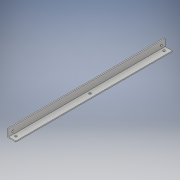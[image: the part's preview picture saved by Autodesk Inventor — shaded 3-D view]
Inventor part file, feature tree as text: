
AUTODESK INVENTOR PART (.ipt)
format: ipt  version: 2017 (Build 210142000, 142)  size: 129,024 bytes
history: native  units: in
note: dims shown in document units (in); Inventor stores cm internally (conversion verified against a paired STEP export)
features: hole x3, sketch x3, extrude x1
ambient origin geometry x8: Origin, YZ Plane, XZ Plane, XY Plane, X Axis, Y Axis, Z Axis, Center Point
bodies: Solid1 (feature_tree)
feature tree (7):
  extrude  "Extrusion1"  Depth=1.0in
  hole  "rail"  [1 undecoded]
  hole  "mount"  [1 undecoded]
  hole  "Hole5"  [1 undecoded]
  sketch  "Sketch2"  dims[d0=1.0in d1=1.0in]
  sketch  "Sketch7"  dims[d2=0.125in d3=19.375in d4=0.0in]
  sketch  "Sketch8"  dims[d5=0.5in d6=0.5in d7=0.7874in d9=18.375in d10=0.3937in d12=1.0in d14=0.266in d15=0.75in d16=0.385in d17=0.25in d18=0.5635in d19=1.0in d20=0.8108in d31=0.5in d43=0.5in d44=0.5in d45=0.7874in d47=18.375in d48=0.3937in d50=1.0in d52=0.266in d53=0.75in d54=0.507in d55=0.25in d56=0.5635in d57=1.0in d58=0.8108in d59=0.266in d60=0.75in d61=0.507in d62=0.25in d63=0.5635in d64=1.0in d65=0.8108in]
note: 3 required parameter values undecoded (feature->parameter linkage not recoverable at this tier; creation-order binding heuristic only, values carry confidence <= 0.55)
